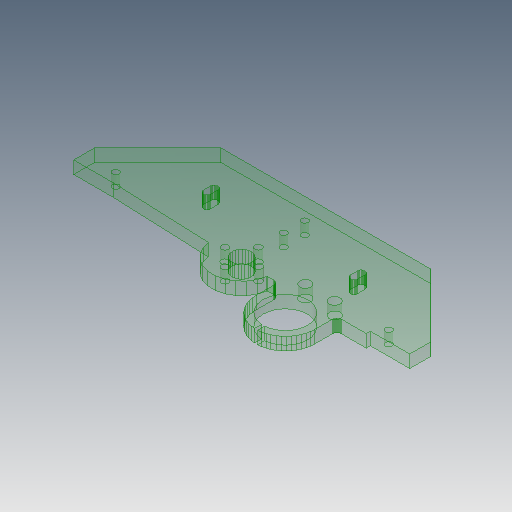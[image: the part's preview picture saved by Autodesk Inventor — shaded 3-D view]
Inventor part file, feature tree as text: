
AUTODESK INVENTOR PART (.ipt)
format: ipt  version: 2017 (Build 210142000, 142)  size: 457,728 bytes
history: native  units: mm
features: sketch x5, other x3
ambient origin geometry x8: Origin, YZ Plane, XZ Plane, XY Plane, X Axis, Y Axis, Z Axis, Center Point
bodies: Solid1 (feature_tree)
feature tree (8):
  other  "Rear-Bed-Holder-Lower.ipt"
  other  "Solid1::Rear-Bed-Holder-Lower.ipt"
  other  "TaggingFeature1"
  sketch  "Sketch1"  dims[d0=10.0mm]
  sketch  "Sketch2"
  sketch  "Sketch3"
  sketch  "Sketch4"
  sketch  "Sketch5"
